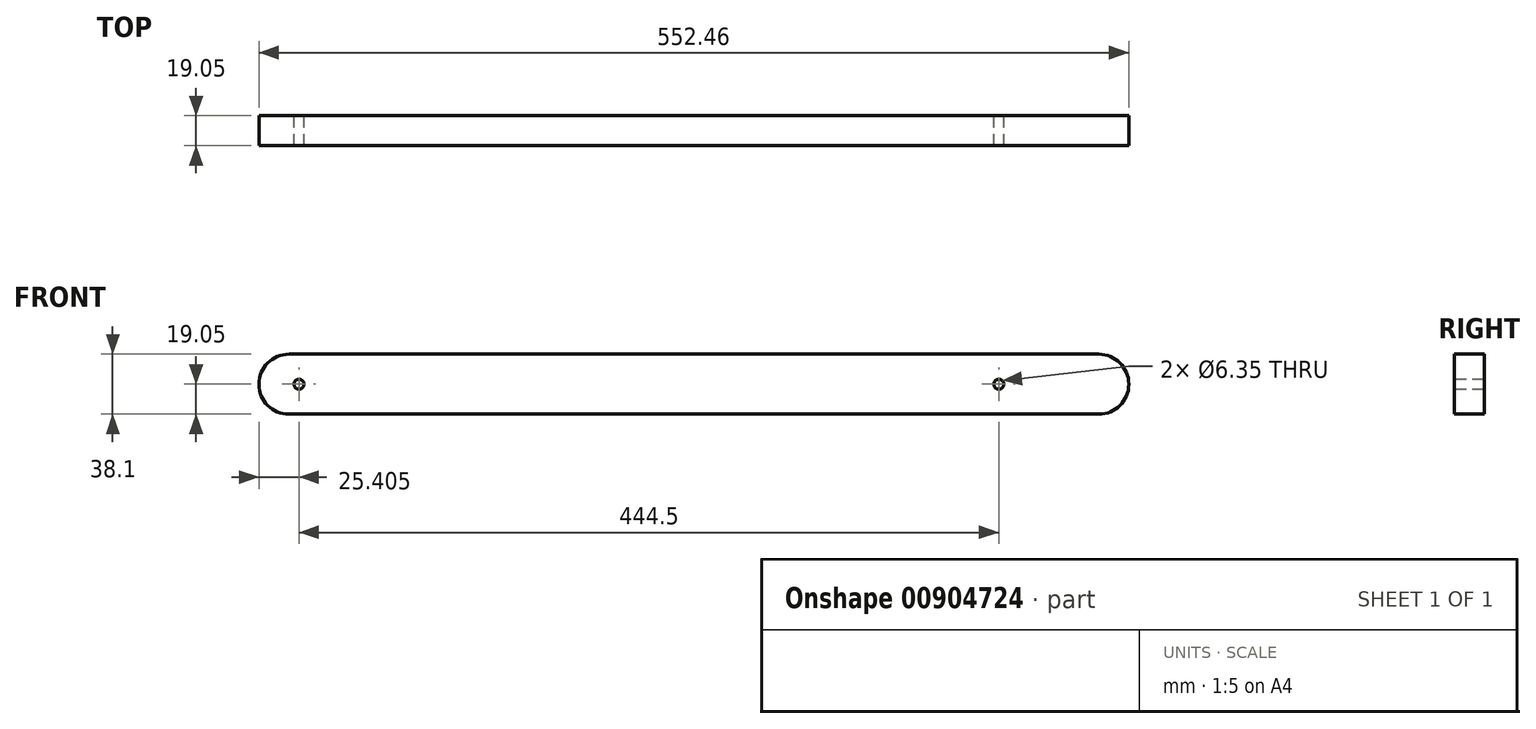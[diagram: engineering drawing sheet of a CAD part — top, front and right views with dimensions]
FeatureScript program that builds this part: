
annotation { "Feature Type Name" : "Feature", "Feature Type Description" : "" }
export const myFeature = defineFeature(function(context is Context, id is Id, definition is map)
    precondition{}
    {
        {
            var Q0;
            Q0=qCreatedBy(makeId("Front.planeOp"),FACE);
            var sketch = newSketch(context, id + "F0", { "sketchPlane" : qUnion([Q0])});
            skLineSegment(sketch, "E0.bottom", {"start": v(-257.18, -19.05) * mm, "end": v(257.18, -19.05) * mm});
            skLineSegment(sketch, "E0.top", {"start": v(-257.18, 19.05) * mm, "end": v(257.18, 19.05) * mm});
            skPoint(sketch, "E0.middle", {"position": v(0, 0) * mm});
            skArc(sketch, "E1", {"start": v(-257.18, 19.05) * mm, "mid": v(-276.23, 0) * mm, "end": v(-257.18, -19.05) * mm});
            skArc(sketch, "E2", {"start": v(257.18, -19.05) * mm, "mid": v(276.23, 0) * mm, "end": v(257.18, 19.05) * mm});
            skPoint(sketch, "E3", {"position": v(-250.83, 0) * mm});
            skPoint(sketch, "E4", {"position": v(193.67, 0) * mm});
            skCircle(sketch, "E5", {"center": v(-250.83, 0) * mm, "radius": 3.18 * mm});
            skCircle(sketch, "E6", {"center": v(193.67, 0) * mm, "radius": 3.18 * mm});
            skSolve(sketch);
        }
        {
            var Q0;
            Q0=makeQuery(id+"F0.imprint","IMPRINT",FACE,{"disambiguationData":[TD([[makeQuery(id+"F0.imprint","IMPRINT",EDGE,{"derivedFrom":sQuery(id+"F0.wireOp",EDGE,"E0.bottom")}),1.0]])]});
            extrude(context, id + "F1", {"entities" : qUnion([Q0]), "depth" : 19.05 * mm, "offsetDistance" : 25.4 * mm});
        }
    });
